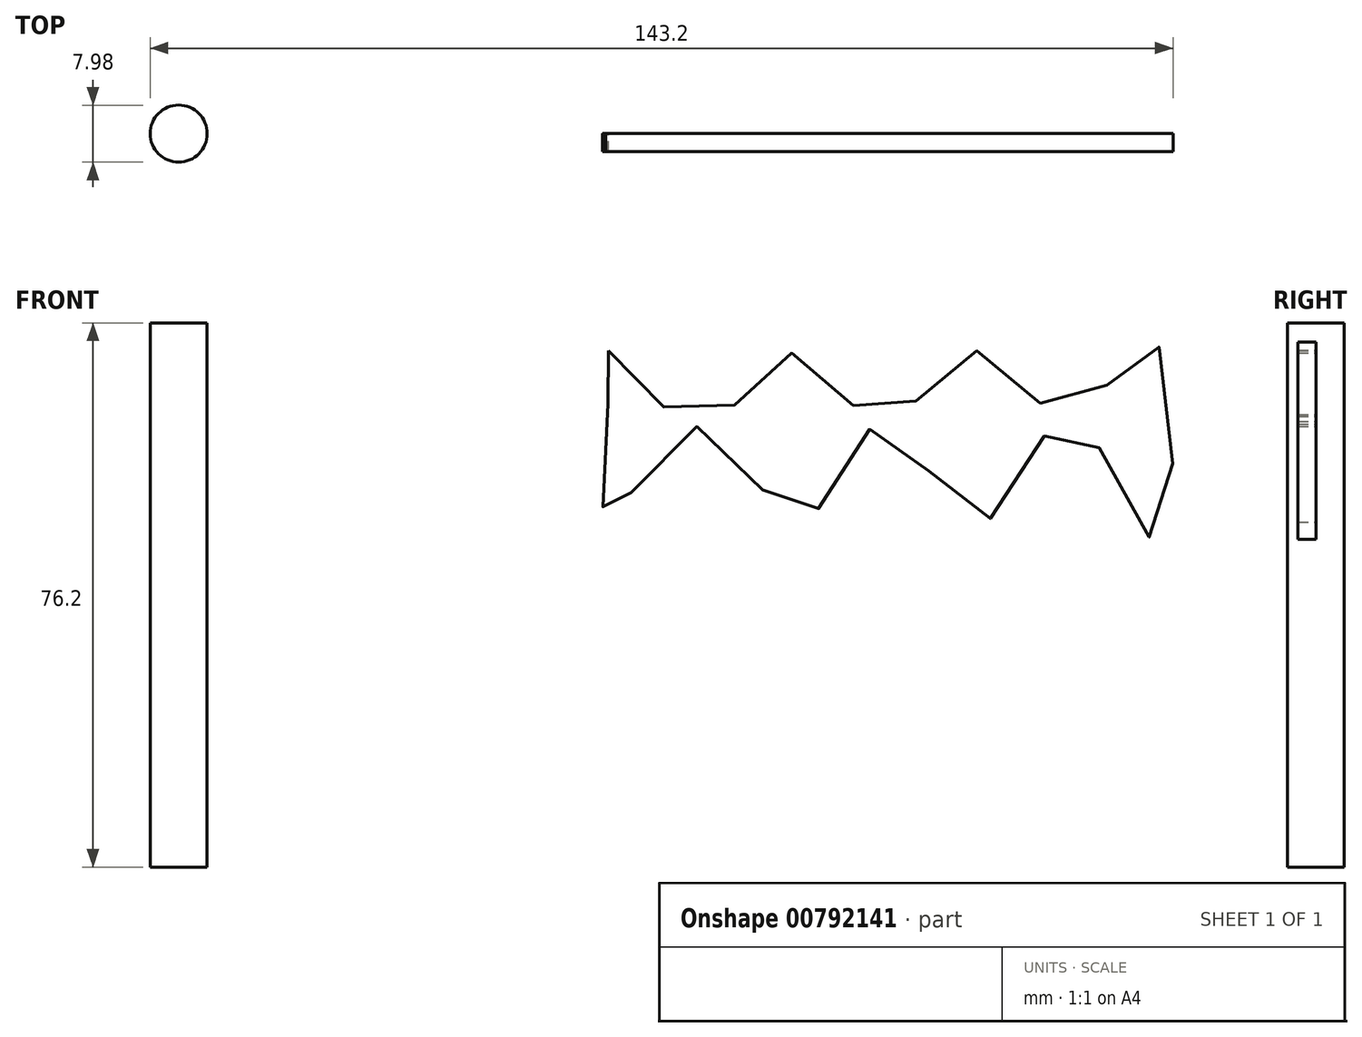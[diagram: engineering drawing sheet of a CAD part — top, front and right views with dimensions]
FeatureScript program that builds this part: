
annotation { "Feature Type Name" : "Feature", "Feature Type Description" : "" }
export const myFeature = defineFeature(function(context is Context, id is Id, definition is map)
    precondition{}
    {
        {
            var Q0;
            Q0=qCreatedBy(makeId("Top.planeOp"),FACE);
            var sketch = newSketch(context, id + "F0", { "sketchPlane" : qUnion([Q0])});
            skCircle(sketch, "E0", {"center": v(-60.14, 0) * mm, "radius": 4 * mm});
            skSolve(sketch);
        }
        {
            var Q0;
            Q0=makeQuery(id+"F0.imprint","IMPRINT",FACE,{"disambiguationData":[TD([[makeQuery(id+"F0.imprint","IMPRINT",EDGE,{"derivedFrom":sQuery(id+"F0.wireOp",EDGE,"E0")}),1.0]])]});
            extrude(context, id + "F1", {"entities" : qUnion([Q0]), "depth" : 76.2 * mm, "offsetDistance" : 25.4 * mm});
        }
        {
            var Q0;
            Q0=qCreatedBy(makeId("Front.planeOp"),FACE);
            var sketch = newSketch(context, id + "F2", { "sketchPlane" : qUnion([Q0])});
            skFitSpline(sketch, "E1", {"points": [v(0, 72.3) * mm, v(13.2, 62.02) * mm, v(25.53, 71.96) * mm, v(38.55, 62.36) * mm, v(51.23, 72.3) * mm, v(64.6, 63.39) * mm, v(76.58, 73.33) * mm, v(76.58, 45.91) * mm, v(64.6, 63.05) * mm, v(52.25, 48.31) * mm, v(38.2, 62.02) * mm, v(26.9, 48.31) * mm, v(12.5, 61.68) * mm, v(0, 48.31) * mm, v(0, 67.5) * mm, v(0, 72.3) * mm]});
            skSolve(sketch);
        }
        {
            var Q0;
            Q0 = qSketchRegion(id + "F2", true);
            extrude(context, id + "F3", {"entities" : qUnion([Q0]), "depth" : 2.54 * mm, "offsetDistance" : 25.4 * mm});
        }
    });
